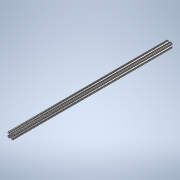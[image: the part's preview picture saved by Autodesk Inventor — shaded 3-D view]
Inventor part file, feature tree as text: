
AUTODESK INVENTOR PART (.ipt)
format: ipt  version: 2020 (Build 240168000, 168)  size: 243,200 bytes
history: native  units: in
note: dims shown in document units (in); Inventor stores cm internally (conversion verified against a paired STEP export)
features: extrude x1, sketch x1
ambient origin geometry x8: Origin, YZ Plane, XZ Plane, XY Plane, X Axis, Y Axis, Z Axis, Center Point
bodies: Solid1 (feature_tree)
feature tree (2):
  extrude  "Extrusion1"  [1 undecoded]
  sketch  "Sketch1"  dims[d0=30.0in d1=0.0in]
note: 1 required parameter value undecoded (feature->parameter linkage not recoverable at this tier; creation-order binding heuristic only, values carry confidence <= 0.55)
